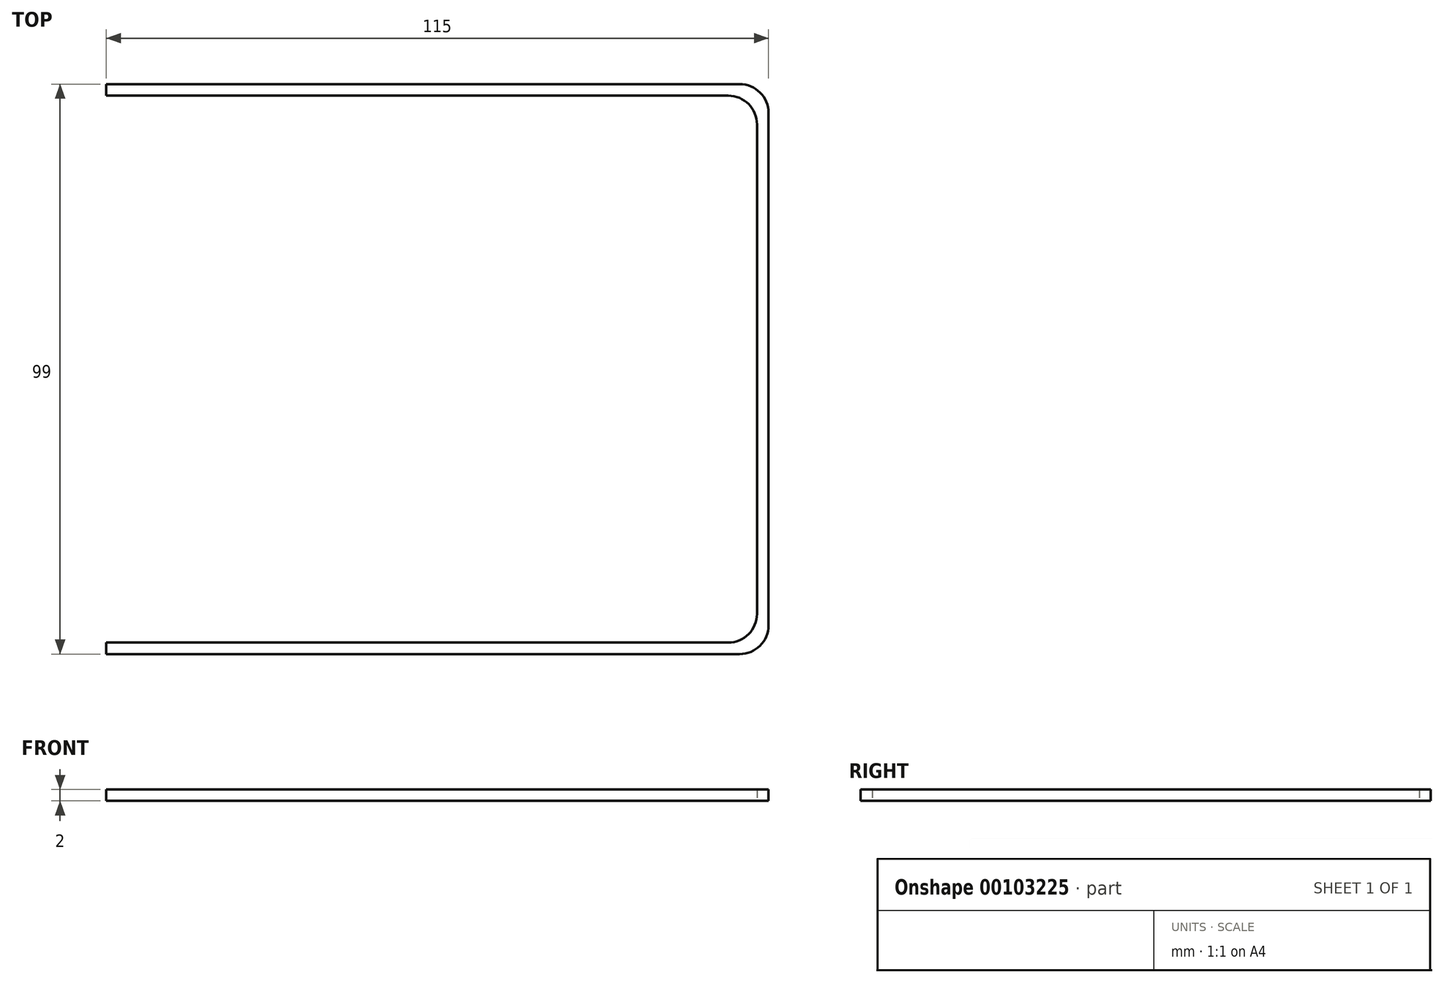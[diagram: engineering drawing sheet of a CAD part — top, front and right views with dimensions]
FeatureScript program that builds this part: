
annotation { "Feature Type Name" : "Feature", "Feature Type Description" : "" }
export const myFeature = defineFeature(function(context is Context, id is Id, definition is map)
    precondition{}
    {
        {
            var Q0;
            Q0=qCreatedBy(makeId("Top.planeOp"),FACE);
            var sketch = newSketch(context, id + "F0", { "sketchPlane" : qUnion([Q0])});
            skLineSegment(sketch, "E0.bottom", {"start": v(95, -60.5) * mm, "end": v(-13, -60.5) * mm});
            skLineSegment(sketch, "E0.top", {"start": v(95, 34.5) * mm, "end": v(-13, 34.5) * mm});
            skLineSegment(sketch, "E0.left", {"start": v(100, -55.5) * mm, "end": v(100, 29.5) * mm});
            skPoint(sketch, "E0.middle", {"position": v(0, 0) * mm});
            skLineSegment(sketch, "E1.1", {"start": v(97, -62.5) * mm, "end": v(-13, -62.5) * mm});
            skLineSegment(sketch, "E1.2", {"start": v(102, -57.5) * mm, "end": v(102, 31.5) * mm});
            skLineSegment(sketch, "E1.3", {"start": v(97, 36.5) * mm, "end": v(-13, 36.5) * mm});
            skPoint(sketch, "E2.visualSharp", {"position": v(102, -62.5) * mm});
            skArc(sketch, "E2.filletArc", {"start": v(97, -62.5) * mm, "mid": v(100.54, -61.04) * mm, "end": v(102, -57.5) * mm});
            skPoint(sketch, "E3.visualSharp", {"position": v(102, 36.5) * mm});
            skArc(sketch, "E3.filletArc", {"start": v(102, 31.5) * mm, "mid": v(100.54, 35.04) * mm, "end": v(97, 36.5) * mm});
            skPoint(sketch, "E4.visualSharp", {"position": v(100, 34.5) * mm});
            skArc(sketch, "E4.filletArc", {"start": v(100, 29.5) * mm, "mid": v(98.54, 33.04) * mm, "end": v(95, 34.5) * mm});
            skPoint(sketch, "E5.visualSharp", {"position": v(100, -60.5) * mm});
            skArc(sketch, "E5.filletArc", {"start": v(95, -60.5) * mm, "mid": v(98.54, -59.04) * mm, "end": v(100, -55.5) * mm});
            skLineSegment(sketch, "E6", {"start": v(-13, 36.5) * mm, "end": v(-13, 34.5) * mm, "construction": true});
            skLineSegment(sketch, "E7", {"start": v(-13, 34.5) * mm, "end": v(-13, 35.5) * mm, "construction": true});
            skLineSegment(sketch, "E8", {"start": v(-13, 35.5) * mm, "end": v(89.5, 35.5) * mm, "construction": true});
            skLineSegment(sketch, "E9", {"start": v(98.54, 33.04) * mm, "end": v(100.54, 35.04) * mm, "construction": true});
            skLineSegment(sketch, "E10", {"start": v(-13, 36.5) * mm, "end": v(-13, 34.5) * mm});
            skLineSegment(sketch, "E11", {"start": v(-13, -60.5) * mm, "end": v(-13, -62.5) * mm});
            skSolve(sketch);
        }
        {
            var Q0;
            Q0=makeQuery(id+"F0.imprint","IMPRINT",FACE,{"disambiguationData":[TD([[makeQuery(id+"F0.imprint","IMPRINT",EDGE,{"derivedFrom":sQuery(id+"F0.wireOp",EDGE,"E0.bottom")}),1.0]])]});
            extrude(context, id + "F1", {"entities" : qUnion([Q0]), "depth" : 2 * mm});
        }
    });
